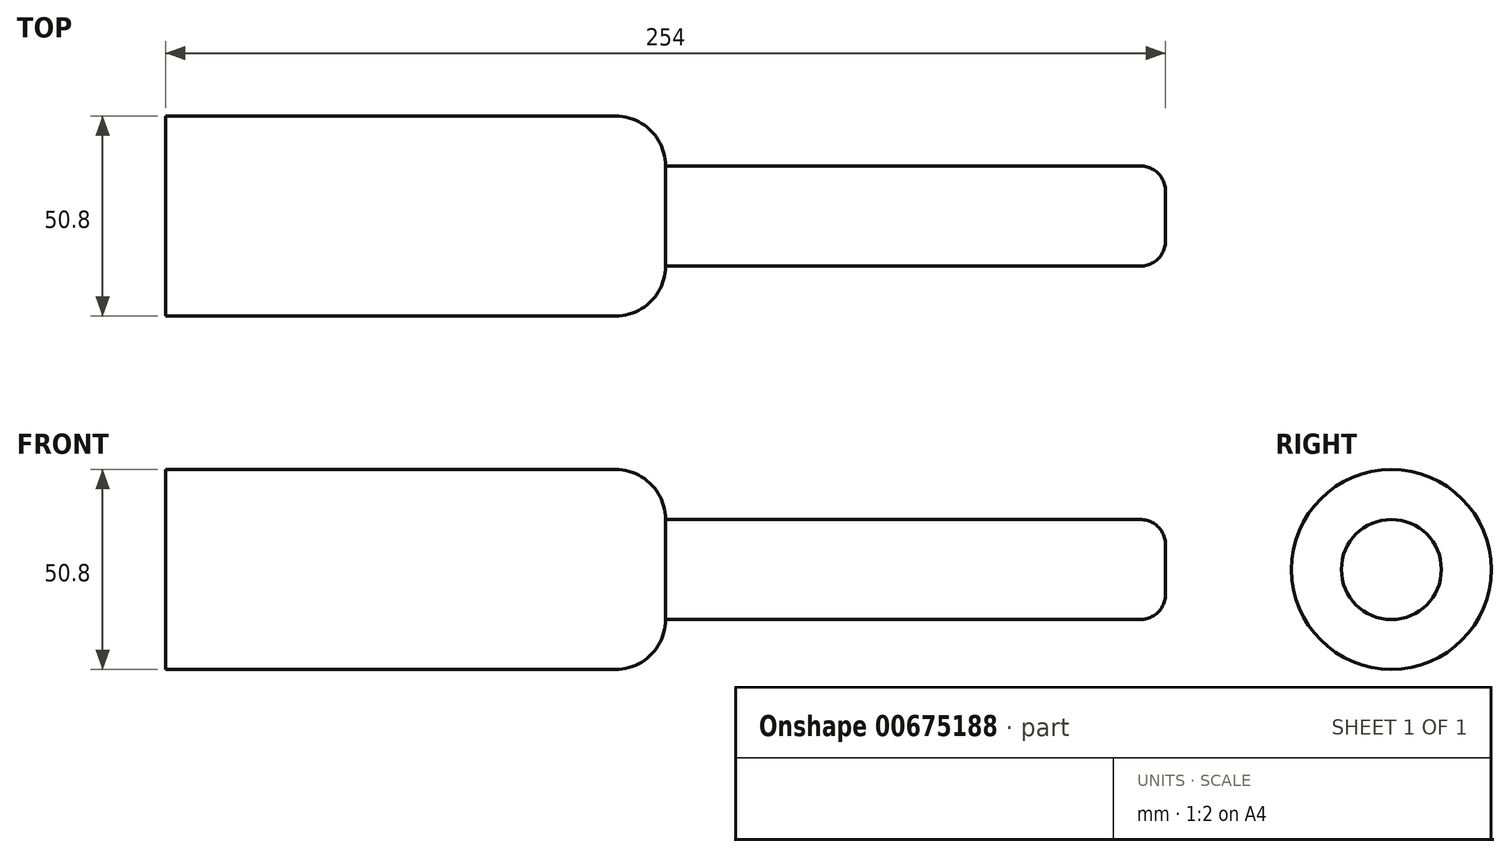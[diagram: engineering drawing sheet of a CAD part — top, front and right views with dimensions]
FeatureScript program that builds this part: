
annotation { "Feature Type Name" : "Feature", "Feature Type Description" : "" }
export const myFeature = defineFeature(function(context is Context, id is Id, definition is map)
    precondition{}
    {
        {
            var Q0;
            Q0=qCreatedBy(makeId("Right.planeOp"),FACE);
            var sketch = newSketch(context, id + "F0", { "sketchPlane" : qUnion([Q0])});
            skLineSegment(sketch, "E0.bottom", {"start": v(0, 25.4) * mm, "end": v(0, 25.4) * mm});
            skLineSegment(sketch, "E0.top", {"start": v(0, -25.4) * mm, "end": v(0, -25.4) * mm});
            skLineSegment(sketch, "E0.left", {"start": v(25.4, 0) * mm, "end": v(25.4, 0) * mm});
            skLineSegment(sketch, "E0.right", {"start": v(-25.4, 0) * mm, "end": v(-25.4, 0) * mm});
            skPoint(sketch, "E0.middle", {"position": v(0, 0) * mm});
            skLineSegment(sketch, "E1.bottom", {"start": v(0, 12.7) * mm, "end": v(0, 12.7) * mm});
            skLineSegment(sketch, "E1.top", {"start": v(0, -12.7) * mm, "end": v(0, -12.7) * mm});
            skLineSegment(sketch, "E1.left", {"start": v(12.7, 0) * mm, "end": v(12.7, 0) * mm});
            skLineSegment(sketch, "E1.right", {"start": v(-12.7, 0) * mm, "end": v(-12.7, 0) * mm});
            skPoint(sketch, "E2.visualSharp", {"position": v(-25.4, 25.4) * mm});
            skArc(sketch, "E2.filletArc", {"start": v(0, 25.4) * mm, "mid": v(-17.96, 17.96) * mm, "end": v(-25.4, 0) * mm});
            skPoint(sketch, "E3.visualSharp", {"position": v(-25.4, -25.4) * mm});
            skArc(sketch, "E3.filletArc", {"start": v(-25.4, 0) * mm, "mid": v(-17.96, -17.96) * mm, "end": v(0, -25.4) * mm});
            skPoint(sketch, "E4.visualSharp", {"position": v(25.4, -25.4) * mm});
            skArc(sketch, "E4.filletArc", {"start": v(0, -25.4) * mm, "mid": v(17.96, -17.96) * mm, "end": v(25.4, 0) * mm});
            skPoint(sketch, "E5.visualSharp", {"position": v(25.4, 25.4) * mm});
            skArc(sketch, "E5.filletArc", {"start": v(25.4, 0) * mm, "mid": v(17.96, 17.96) * mm, "end": v(0, 25.4) * mm});
            skPoint(sketch, "E6.visualSharp", {"position": v(-12.7, 12.7) * mm});
            skArc(sketch, "E6.filletArc", {"start": v(0, 12.7) * mm, "mid": v(-8.98, 8.98) * mm, "end": v(-12.7, 0) * mm});
            skPoint(sketch, "E7.visualSharp", {"position": v(-12.7, -12.7) * mm});
            skArc(sketch, "E7.filletArc", {"start": v(-12.7, 0) * mm, "mid": v(-8.98, -8.98) * mm, "end": v(0, -12.7) * mm});
            skPoint(sketch, "E8.visualSharp", {"position": v(12.7, -12.7) * mm});
            skArc(sketch, "E8.filletArc", {"start": v(0, -12.7) * mm, "mid": v(8.98, -8.98) * mm, "end": v(12.7, 0) * mm});
            skPoint(sketch, "E9.visualSharp", {"position": v(12.7, 12.7) * mm});
            skArc(sketch, "E9.filletArc", {"start": v(12.7, 0) * mm, "mid": v(8.98, 8.98) * mm, "end": v(0, 12.7) * mm});
            skLineSegment(sketch, "E10", {"start": v(-25.4, 25.4) * mm, "end": v(25.4, 25.4) * mm});
            skLineSegment(sketch, "E11", {"start": v(25.4, -25.4) * mm, "end": v(25.4, 25.4) * mm});
            skLineSegment(sketch, "E12", {"start": v(25.4, -25.4) * mm, "end": v(-25.4, -25.4) * mm});
            skLineSegment(sketch, "E13", {"start": v(-25.4, 25.4) * mm, "end": v(-25.4, -25.4) * mm});
            skLineSegment(sketch, "E14", {"start": v(-12.7, -12.7) * mm, "end": v(-12.7, 12.7) * mm});
            skLineSegment(sketch, "E15", {"start": v(12.7, 12.7) * mm, "end": v(-12.7, 12.7) * mm});
            skLineSegment(sketch, "E16", {"start": v(12.7, -12.7) * mm, "end": v(12.7, 12.7) * mm});
            skLineSegment(sketch, "E17", {"start": v(12.7, -12.7) * mm, "end": v(-12.7, -12.7) * mm});
            skSolve(sketch);
        }
        {
            var Q0;
            Q0=makeQuery(id+"F0.imprint","IMPRINT",FACE,{"disambiguationData":[TD([[makeQuery(id+"F0.imprint","IMPRINT",EDGE,{"derivedFrom":sQuery(id+"F0.wireOp",EDGE,"E6.filletArc")}),1.0]])]});
            extrude(context, id + "F1", {"entities" : qUnion([Q0]), "depth" : 254 * mm, "offsetDistance" : 25.4 * mm});
        }
        {
            var Q0;
            {var subQ0=sQuery(id+"F0.wireOp",EDGE,"E6.filletArc");Q0=makeQuery(id+"F0.imprint","IMPRINT",FACE,{"disambiguationData":[TD([[makeQuery(id+"F0.imprint","IMPRINT",EDGE,{"derivedFrom":subQ0}),-1.0]])]});}
            var Q1;
            {var subQ0=sQuery(id+"F0.wireOp",EDGE,"E9.filletArc");Q1=makeQuery(id+"F0.imprint","IMPRINT",FACE,{"disambiguationData":[TD([[makeQuery(id+"F0.imprint","IMPRINT",EDGE,{"derivedFrom":subQ0}),-1.0]])]});}
            var Q2;
            {var subQ0=sQuery(id+"F0.wireOp",EDGE,"E8.filletArc");Q2=makeQuery(id+"F0.imprint","IMPRINT",FACE,{"disambiguationData":[TD([[makeQuery(id+"F0.imprint","IMPRINT",EDGE,{"derivedFrom":subQ0}),-1.0]])]});}
            var Q3;
            {var subQ0=sQuery(id+"F0.wireOp",EDGE,"E7.filletArc");Q3=makeQuery(id+"F0.imprint","IMPRINT",FACE,{"disambiguationData":[TD([[makeQuery(id+"F0.imprint","IMPRINT",EDGE,{"derivedFrom":subQ0}),-1.0]])]});}
            extrude(context, id + "F2", {"entities" : qUnion([Q0, Q1, Q2, Q3]), "operationType" : NewBodyOperationType.ADD, "depth" : 190.5 * mm, "offsetDistance" : 25.4 * mm});
        }
        {
            var Q0;
            Q0=makeQuery(id+"F0.imprint","IMPRINT",FACE,{"disambiguationData":[TD([[makeQuery(id+"F0.imprint","IMPRINT",EDGE,{"derivedFrom":sQuery(id+"F0.wireOp",EDGE,"E2.filletArc")}),1.0]])]});
            extrude(context, id + "F3", {"entities" : qUnion([Q0]), "operationType" : NewBodyOperationType.ADD, "depth" : 127 * mm, "offsetDistance" : 25.4 * mm});
        }
        {
            var Q0;
            {var subQ0=sQuery(id+"F0.wireOp",EDGE,"E2.filletArc");Q0=makeQuery(id+"F0.imprint","IMPRINT",FACE,{"disambiguationData":[TD([[makeQuery(id+"F0.imprint","IMPRINT",EDGE,{"derivedFrom":subQ0}),-1.0]])]});}
            var Q1;
            {var subQ0=sQuery(id+"F0.wireOp",EDGE,"E3.filletArc");Q1=makeQuery(id+"F0.imprint","IMPRINT",FACE,{"disambiguationData":[TD([[makeQuery(id+"F0.imprint","IMPRINT",EDGE,{"derivedFrom":subQ0}),-1.0]])]});}
            var Q2;
            {var subQ0=sQuery(id+"F0.wireOp",EDGE,"E4.filletArc");Q2=makeQuery(id+"F0.imprint","IMPRINT",FACE,{"disambiguationData":[TD([[makeQuery(id+"F0.imprint","IMPRINT",EDGE,{"derivedFrom":subQ0}),-1.0]])]});}
            var Q3;
            {var subQ0=sQuery(id+"F0.wireOp",EDGE,"E5.filletArc");Q3=makeQuery(id+"F0.imprint","IMPRINT",FACE,{"disambiguationData":[TD([[makeQuery(id+"F0.imprint","IMPRINT",EDGE,{"derivedFrom":subQ0}),-1.0]])]});}
            extrude(context, id + "F4", {"entities" : qUnion([Q0, Q1, Q2, Q3]), "operationType" : NewBodyOperationType.ADD, "depth" : 63.5 * mm, "offsetDistance" : 25.4 * mm});
        }
        {
            var Q0;
            Q0=makeQuery(id+"F2.opExtrude","SWEPT_EDGE",EDGE,{"disambiguationData":[OSD([sQuery(id+"F0.wireOp",EDGE,"E14"),sQuery(id+"F0.wireOp",EDGE,"E17")])]});
            var Q1;
            Q1=makeQuery(id+"F2.opExtrude","SWEPT_EDGE",EDGE,{"disambiguationData":[OSD([sQuery(id+"F0.wireOp",EDGE,"E16"),sQuery(id+"F0.wireOp",EDGE,"E17")])]});
            var Q2;
            Q2=makeQuery(id+"F2.opExtrude","SWEPT_EDGE",EDGE,{"disambiguationData":[OSD([sQuery(id+"F0.wireOp",EDGE,"E15"),sQuery(id+"F0.wireOp",EDGE,"E16")])]});
            var Q3;
            Q3=makeQuery(id+"F2.opExtrude","SWEPT_EDGE",EDGE,{"disambiguationData":[OSD([sQuery(id+"F0.wireOp",EDGE,"E14"),sQuery(id+"F0.wireOp",EDGE,"E15")])]});
            fillet(context, id + "F5", {"entities" : qUnion([Q0, Q1, Q2, Q3]), "tangentPropagation" : true, "radius" : 12.7 * mm, "defaultsChanged" : true, "vertexSettings" : [], "allowEdgeOverflow" : false});
        }
        {
            var Q0;
            Q0=makeQuery(id+"F4.opExtrude","SWEPT_EDGE",EDGE,{"disambiguationData":[OSD([sQuery(id+"F0.wireOp",EDGE,"E12"),sQuery(id+"F0.wireOp",EDGE,"E13")])]});
            var Q1;
            Q1=makeQuery(id+"F4.opExtrude","SWEPT_EDGE",EDGE,{"disambiguationData":[OSD([sQuery(id+"F0.wireOp",EDGE,"E11"),sQuery(id+"F0.wireOp",EDGE,"E12")])]});
            var Q2;
            Q2=makeQuery(id+"F4.opExtrude","SWEPT_EDGE",EDGE,{"disambiguationData":[OSD([sQuery(id+"F0.wireOp",EDGE,"E10"),sQuery(id+"F0.wireOp",EDGE,"E13")])]});
            var Q3;
            Q3=makeQuery(id+"F4.opExtrude","SWEPT_EDGE",EDGE,{"disambiguationData":[OSD([sQuery(id+"F0.wireOp",EDGE,"E10"),sQuery(id+"F0.wireOp",EDGE,"E11")])]});
            fillet(context, id + "F6", {"entities" : qUnion([Q0, Q1, Q2, Q3]), "tangentPropagation" : true, "radius" : 25.4 * mm, "defaultsChanged" : true, "vertexSettings" : [], "allowEdgeOverflow" : false});
        }
        {
            var Q0;
            Q0=makeQuery(id+"F3.opExtrude","CAP_EDGE",EDGE,{"disambiguationData":[OSD([sQuery(id+"F0.wireOp",EDGE,"E2.filletArc"),sQuery(id+"F0.wireOp",EDGE,"E3.filletArc"),sQuery(id+"F0.wireOp",EDGE,"E4.filletArc"),sQuery(id+"F0.wireOp",EDGE,"E5.filletArc")])],"isStart":false});
            fillet(context, id + "F7", {"entities" : qUnion([Q0]), "tangentPropagation" : true, "radius" : 12.7 * mm, "defaultsChanged" : true, "vertexSettings" : [], "allowEdgeOverflow" : false});
        }
        {
            var Q0;
            Q0=makeQuery(id+"F1.opExtrude","CAP_FACE",FACE,{"disambiguationData":[OSD([sQuery(id+"F0.wireOp",EDGE,"E6.filletArc"),sQuery(id+"F0.wireOp",EDGE,"E7.filletArc"),sQuery(id+"F0.wireOp",EDGE,"E8.filletArc"),sQuery(id+"F0.wireOp",EDGE,"E9.filletArc")])],"isStart":false});
            fillet(context, id + "F8", {"entities" : qUnion([Q0]), "tangentPropagation" : true, "radius" : 6.35 * mm, "defaultsChanged" : true, "vertexSettings" : [], "allowEdgeOverflow" : false});
        }
    });
